# Revit family: РД1
name_source: partatom
category: Соединительные детали воздуховодов
units: mm (PartAtom-declared; Revit-internal decimal feet)

## family parameters
Всегда вертикально = Да
На основе рабочей плоскости = Нет
Общий = Нет
При загрузке вырезать с полостями = Нет
Размер круглого соединителя = Использовать диаметр
Тип детали = Отвод

## types (25) — shared parameters
00_20_Manufacturer = Вентс
00_20_Name = Решітка димовидалення
C = 34 мм
Casing Material = Сталь, гальванизированная
D = 27 мм
D1 = 2 мм
D2 = 6 мм
Load Classification = HVAC
Maintenance zone material = <По категории>
Maximum Air Flow = 0.0 м³/ч
S = 40 мм
URL = https://vents.ua
r = 2 мм
t = 8 мм
Изготовитель = Вентс
Ширина = 27 мм
zero-valued in all types: Отметка по умолчанию

## per-type parameters (varying)
| type | A | A1 | A2 | B | B1 | B2 | a1 | a2 | n | Вага | Высота | Длинна |
| РД1 300х300 | 367 мм | 300 мм | 334 мм | 367 мм | 300 мм | 334 мм | 150 мм | -150 мм | 8 | 1.29 кг | 367 мм | 367 мм |
| РД1 350х300 | 417 мм | 350 мм | 384 мм | 367 мм | 300 мм | 334 мм | 175 мм | -175 мм | 8 | 1.46 кг | 367 мм | 417 мм |
| РД1 400х300 | 467 мм | 400 мм | 434 мм | 367 мм | 300 мм | 334 мм | 200 мм | -200 мм | 8 | 1.63 кг | 367 мм | 467 мм |
| РД1 450х300 | 517 мм | 450 мм | 484 мм | 367 мм | 300 мм | 334 мм | 225 мм | -225 мм | 8 | 1.80 кг | 367 мм | 517 мм |
| РД1 500х300 | 567 мм | 500 мм | 534 мм | 367 мм | 300 мм | 334 мм | 250 мм | -250 мм | 8 | 1.97 кг | 367 мм | 567 мм |
| РД1 550х300 | 617 мм | 550 мм | 584 мм | 367 мм | 300 мм | 334 мм | 275 мм | -275 мм | 8 | 2.14 кг | 367 мм | 617 мм |
| РД1 600х300 | 667 мм | 600 мм | 634 мм | 367 мм | 300 мм | 334 мм | 300 мм | -300 мм | 8 | 2.32 кг | 367 мм | 667 мм |
| РД1 650х300 | 717 мм | 650 мм | 684 мм | 367 мм | 300 мм | 334 мм | 325 мм | -325 мм | 8 | 2.49 кг | 367 мм | 717 мм |
| РД1 700х300 | 767 мм | 700 мм | 734 мм | 367 мм | 300 мм | 334 мм | 350 мм | -350 мм | 8 | 2.66 кг | 367 мм | 767 мм |
| РД1 750х300 | 817 мм | 750 мм | 784 мм | 367 мм | 300 мм | 334 мм | 375 мм | -375 мм | 8 | 2.83 кг | 367 мм | 817 мм |
| РД1 800х300 | 867 мм | 800 мм | 834 мм | 367 мм | 300 мм | 334 мм | 400 мм | -400 мм | 8 | 3.00 кг | 367 мм | 867 мм |
| РД1 850х300 | 917 мм | 850 мм | 884 мм | 367 мм | 300 мм | 334 мм | 425 мм | -425 мм | 8 | 3.17 кг | 367 мм | 917 мм |
| РД1 900х300 | 967 мм | 900 мм | 934 мм | 367 мм | 300 мм | 334 мм | 450 мм | -450 мм | 8 | 3.34 кг | 367 мм | 967 мм |
| РД1 950х300 | 1017 мм | 950 мм | 984 мм | 367 мм | 300 мм | 334 мм | 475 мм | -475 мм | 8 | 3.51 кг | 367 мм | 1017 мм |
| РД1 1000х300 | 1067 мм | 1000 мм | 1034 мм | 367 мм | 300 мм | 334 мм | 500 мм | -500 мм | 8 | 3.68 кг | 367 мм | 1067 мм |
| РД1 1000х350 | 1067 мм | 1000 мм | 1034 мм | 417 мм | 350 мм | 384 мм | 500 мм | -500 мм | 9 | 4.17 кг | 417 мм | 1067 мм |
| РД1 1000х400 | 1067 мм | 1000 мм | 1034 мм | 467 мм | 400 мм | 434 мм | 500 мм | -500 мм | 10 | 4.65 кг | 467 мм | 1067 мм |
| РД1 1000х450 | 1067 мм | 1000 мм | 1034 мм | 517 мм | 450 мм | 484 мм | 500 мм | -500 мм | 11 | 5.12 кг | 517 мм | 1067 мм |
| РД1 1000х500 | 1067 мм | 1000 мм | 1034 мм | 567 мм | 500 мм | 534 мм | 500 мм | -500 мм | 13 | 5.60 кг | 567 мм | 1067 мм |
| РД1 1000х550 | 1067 мм | 1000 мм | 1034 мм | 617 мм | 550 мм | 584 мм | 500 мм | -500 мм | 14 | 5.09 кг | 617 мм | 1067 мм |
| РД1 600х600 | 667 мм | 600 мм | 634 мм | 667 мм | 600 мм | 634 мм | 300 мм | -300 мм | 15 | 4.14 кг | 667 мм | 667 мм |
| РД1 700х700 | 767 мм | 700 мм | 734 мм | 767 мм | 700 мм | 734 мм | 350 мм | -350 мм | 18 | 5.44 кг | 767 мм | 767 мм |
| РД1 800х800 | 867 мм | 800 мм | 834 мм | 867 мм | 800 мм | 834 мм | 400 мм | -400 мм | 20 | 6.93 кг | 867 мм | 867 мм |
| РД1 900х900 | 967 мм | 900 мм | 934 мм | 967 мм | 900 мм | 934 мм | 450 мм | -450 мм | 23 | 8.60 кг | 967 мм | 967 мм |
| РД1 1000х1000 | 1067 мм | 1000 мм | 1034 мм | 1067 мм | 1000 мм | 1034 мм | 500 мм | -500 мм | 25 | 10.45 кг | 1067 мм | 1067 мм |

note: column(s) folded — value = type name in every type: 00_20_Type
